# Revit family: Porta_LEVEL_B2
name_source: partatom
category: Drzwi
revit_build: Autodesk Revit 2016 (Build: 20150714_1515(x64)
units: mm (PartAtom-declared; Revit-internal decimal feet)

## family parameters
Obiekt nadrzędny = Ściana
Punkt obliczania pomieszczeń = Nie
Tnij formami wycięć po wczytaniu = Nie
Współdzielony = Nie
Zawsze pionowo = Tak

## types (1)
- PN 80
    Funkcja = Wewnętrzna
    Hs = 2017 mm  [stored 6.61745 ft]
    Informacja = Własność Porta KMI Poland, wszelkie prawa zastrzeżone.
    Konstrukcja analityczna = <Brak>
    Materiał_paski = <Wg kategorii>
    Materiał_skrzydło_2 = <Wg kategorii>
    Model = Porta LEVEL
    Producent = PORTA KMI POLAND
    Ss = 818 mm  [stored 2.68373 ft]
    Szerokość = 802 mm
    Szerokość brutto = 880 mm  [stored 2.88714 ft]
    URL = www.porta.com.pl
    Wysokość = 2016 mm
    Wysokość brutto = 2055 mm  [stored 6.74213 ft]
    Zakończenie ściany = Wg obiektu nadrzędnego

note: [stored X ft] marks values corroborated as IEEE doubles in the binary element streams (Revit-internal decimal feet)

## geometry (parser evidence)
native form markers: Blend x4, Sweep x3
no freeform markers — native parametric forms only
